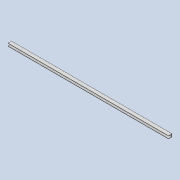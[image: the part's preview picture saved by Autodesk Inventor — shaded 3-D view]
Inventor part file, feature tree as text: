
AUTODESK INVENTOR PART (.ipt)
format: ipt  version: 2020 (Build 240168000, 168)  size: 84,480 bytes
history: native  units: mm
features: extrude x2, sketch x2
ambient origin geometry x8: Origin, YZ Plane, XZ Plane, XY Plane, X Axis, Y Axis, Z Axis, Center Point
bodies: Solid1 (feature_tree)
feature tree (4):
  extrude  "Extrusion1"  Depth=4.0mm
  extrude  "Extrusion2"  Depth=3.2mm
  sketch  "Sketch1"  dims[d0=230.0mm d1=4.0mm]
  sketch  "Sketch2"  dims[d2=5.0mm d3=0.0mm d4=3.2mm d5=4.5mm d6=0.0mm]
